# Revit family: IS_CerafineO_BC750_BIM_GB
name_source: partatom
category: Plumbing Fixtures
units: mm (PartAtom-declared; Revit-internal decimal feet)

## family parameters
Always vertical = No
Cut with Voids When Loaded = No
OmniClass Number = 23.45.55.17
OmniClass Title = Mixing Faucets
Part Type = Normal
Room Calculation Point = No
Round Connector Dimension = Use Diameter
Shared = No
Work Plane-Based = No

## types (2) — shared parameters
Accessories = https://www.idealspec.co.uk
AreaUnits = millimeters
AssetType = Fixed
BIMObjectName = ISI_IdealStandard_Shower mixers_CerafineO_BC750
BIMobject category = Taps & Mixers
BIMobject category code = sanitary-taps-mixers
BIMobject main category = Sanitary
BIMobject main category code = sanitary
Brand = Ideal Standard
Brand url = http://www.idealstandard.co.uk
ConnectionType = Plumbing
CurrencyUnit = £
CurrentRevision = 1
Date of publishing = 09/09/2020
DurationUnit = Year
Edition number = 1
ExpectedLife = 30
FaucetFunction = MIXED
FaucetOperation = OTHER
FaucetType = OTHER
Features = Single, metal lever basin mixer DN 15 with 136 mm spout projection with read / blue marking, 155 mm height Metal aerator, short design and pressure-independent
Help = https://www.idealspec.co.uk
IFC Classification = Sanitary Terminal
IfcExportAs = IfcValveType
IfcExportType = FAUCET
Installation instructions = https://www.idealspec.co.uk
InstallationInstructions = https://www.idealspec.co.uk
IsHighPressure = No
LinearUnits = millimeters
MainColor = Matt Black
MaintenanceInformation = https://www.idealspec.co.uk
Manufacturer = Ideal Standard
Manufacturer name = Ideal Standard
ManufacturerURL = https://www.idealspec.co.uk
Material = Brass
Material main = Brass
ModelNumber = BC750U4
ModelReference = CERAFINE O SH MXR MBLK/CHR SL & WBWS
NBS Reference Code = 45-35-70/335
NBS Reference Description = Shower mixers
Name = Shower mixers_CerafineO_BC750_IdealStandard
NettWeight = 6,40 KG
NominalDepth = 498 mm
NominalHeight = 1394 mm
NominalLength = 498 mm
NominalWidth = 382 mm
OmniClass Code = 23.45.55.17
OmniClass Description = Mixing Faucets
Product Guid = be6eacf6-3c12-46ba-8783-da66ea11d61a
Product SKU = BC750
Product certification = https://www.idealspec.co.uk
Product data url = https://bimobject.com
Product family = CERAFINE MODEL O
Product group = SHOWER SYSTEM
Product name = A_CERAFINE O SH MXR MBLK/CHR SL & WBWS
Product url = https://www.idealspec.co.uk
ProductInformation = https://www.idealspec.co.uk
QR code = http://bimobject.com
Shape = Sculptured
Size = 382 x 499 x 1394 mm
Space = Internal
SpareParts = https://fastpart-spares.co.uk
Technical description = https://www.idealspec.co.uk
TestPressure = 10 bar
UNSPSC Code = 30181700
URL = https://www.idealspec.co.uk
Uniclass 1.4 Code = L725111
Uniclass 1.4 Description = Mixer taps
Uniclass 2.0 Code = Pr_40_30_96_81
Uniclass 2.0 Description = Shower Thermostatic Water Supply Sets
Uniclass 2015 Code = Pr_40_20_87_78
Uniclass 2015 Name = Shower manual water supply sets
Uniclass2015Code = Pr_40_20_87_78
Uniclass2015Title = Shower manual water supply sets
Uniclass2015Version = v1.20
ValveMechanism = Thermostatic
ValveOperation = Lever
Version = 1
VolumeUnits = Litres
WRASURL = https://www.wras.co.uk
WarrantyDescription = Manufacturers Warranty
WarrantyDurationParts = 5
WarrantyDurationUnit = Year
WarrantyGuarantorParts = https://www.idealspec.co.uk
zero-valued in all types: MaterialThickness

## per-type parameters (varying)
| type | BarCode | Color | Description | Finish | GTIN code | Model |
| BC750AA - CERAFINE O HAND SHOWER SPRAY MIXER SL EXPOSED - CHROME | 3800861107132 | Chrome | CERAFINE O HAND SHOWER SPRAY MIXER SL EXPOSED - Chrome | Chrome | https://3800861107132 | BC750AA |
| BC750XG - CERAFINE O HAND SHOWER SPRAY MIXER SL EXPOSED - SILK BLACK | 3800861101093 | Silk Black | CERAFINE O HAND SHOWER SPRAY MIXER SL EXPOSED - Silk Black | Silk Black | https://3800861101093 | BC750XG |

## geometry (parser evidence)
native form markers: Sweep x2
no freeform markers — native parametric forms only
